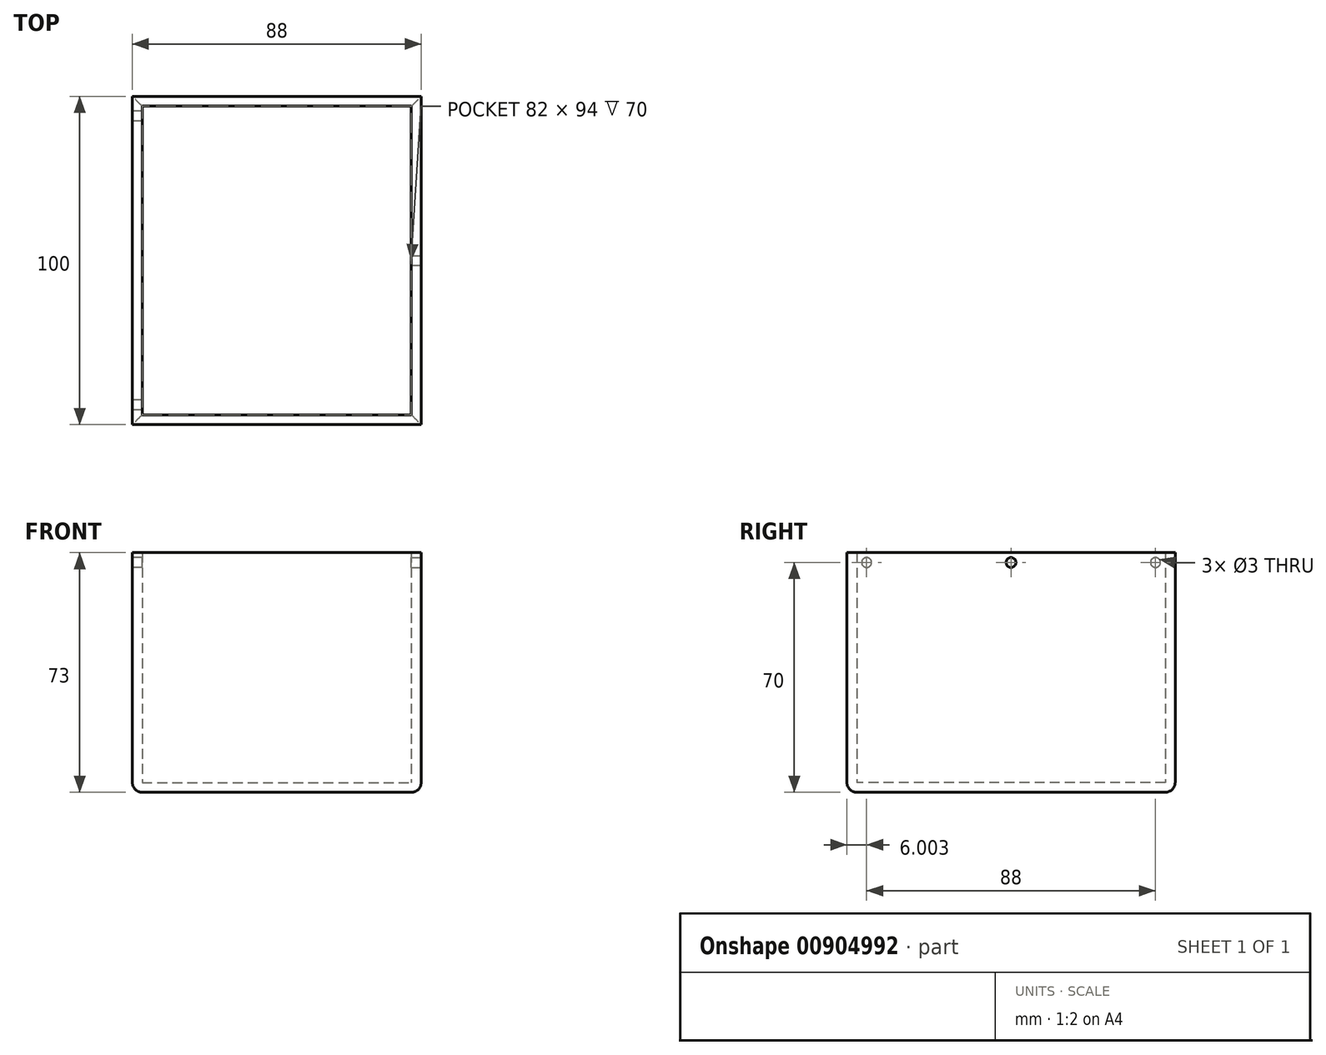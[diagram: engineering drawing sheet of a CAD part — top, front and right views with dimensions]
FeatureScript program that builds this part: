
annotation { "Feature Type Name" : "Feature", "Feature Type Description" : "" }
export const myFeature = defineFeature(function(context is Context, id is Id, definition is map)
    precondition{}
    {
        {
            var Q0;
            Q0=qCreatedBy(makeId("Top.planeOp"),FACE);
            var sketch = newSketch(context, id + "F0", { "sketchPlane" : qUnion([Q0])});
            skLineSegment(sketch, "E0.bottom", {"start": v(-35.32, 52.62) * mm, "end": v(52.68, 52.62) * mm});
            skLineSegment(sketch, "E0.top", {"start": v(-35.32, -47.38) * mm, "end": v(52.68, -47.38) * mm});
            skLineSegment(sketch, "E0.left", {"start": v(-35.32, 52.62) * mm, "end": v(-35.32, -47.38) * mm});
            skLineSegment(sketch, "E0.right", {"start": v(52.68, 52.62) * mm, "end": v(52.68, -47.38) * mm});
            skSolve(sketch);
        }
        {
            var Q0;
            Q0=makeQuery(id+"F0.imprint","IMPRINT",FACE,{"disambiguationData":[TD([[makeQuery(id+"F0.imprint","IMPRINT",EDGE,{"derivedFrom":sQuery(id+"F0.wireOp",EDGE,"E0.bottom")}),-1.0]])]});
            var sketch = newSketch(context, id + "F1", { "sketchPlane" : qUnion([Q0])});
            skLineSegment(sketch, "E1.0", {"start": v(-35.32, 52.62) * mm, "end": v(52.68, 52.62) * mm});
            skLineSegment(sketch, "E1.1", {"start": v(-35.32, 52.62) * mm, "end": v(-35.32, -47.38) * mm});
            skLineSegment(sketch, "E1.2", {"start": v(52.68, 52.62) * mm, "end": v(52.68, -47.38) * mm});
            skLineSegment(sketch, "E1.3", {"start": v(-35.32, -47.38) * mm, "end": v(52.68, -47.38) * mm});
            skLineSegment(sketch, "E2.bottom", {"start": v(-32.32, 49.62) * mm, "end": v(49.68, 49.62) * mm});
            skLineSegment(sketch, "E2.top", {"start": v(-32.32, -44.38) * mm, "end": v(49.68, -44.38) * mm});
            skLineSegment(sketch, "E2.left", {"start": v(-32.32, 49.62) * mm, "end": v(-32.32, -44.38) * mm});
            skLineSegment(sketch, "E2.right", {"start": v(49.68, 49.62) * mm, "end": v(49.68, -44.38) * mm});
            skSolve(sketch);
        }
        {
            var Q0;
            Q0 = qSketchRegion(id + "F0", true);
            extrude(context, id + "F2", {"entities" : qUnion([Q0]), "depth" : -3 * mm, "offsetDistance" : 25 * mm});
        }
        {
            var Q0;
            Q0 = qSketchRegion(id + "F1", true);
            extrude(context, id + "F3", {"entities" : qUnion([Q0]), "operationType" : NewBodyOperationType.ADD, "depth" : 70 * mm, "offsetDistance" : 25 * mm});
        }
        {
            var Q0;
            Q0=makeQuery(id+"F2.opExtrude","CAP_EDGE",EDGE,{"disambiguationData":[OSD([sQuery(id+"F0.wireOp",EDGE,"E0.left")])],"isStart":false});
            var Q1;
            Q1=makeQuery(id+"F2.opExtrude","CAP_EDGE",EDGE,{"disambiguationData":[OSD([sQuery(id+"F0.wireOp",EDGE,"E0.bottom")])],"isStart":false});
            var Q2;
            Q2=makeQuery(id+"F2.opExtrude","CAP_EDGE",EDGE,{"disambiguationData":[OSD([sQuery(id+"F0.wireOp",EDGE,"E0.top")])],"isStart":false});
            var Q3;
            Q3=makeQuery(id+"F2.opExtrude","CAP_EDGE",EDGE,{"disambiguationData":[OSD([sQuery(id+"F0.wireOp",EDGE,"E0.right")])],"isStart":false});
            fillet(context, id + "F4", {"entities" : qUnion([Q0, Q1, Q2, Q3]), "radius" : 3 * mm, "tangentPropagation" : true, "allowEdgeOverflow" : false});
        }
        {
            var Q0;
            Q0=makeQuery(id+"F3.boolean.opBoolean","MERGE",FACE,{"derivedFrom":[makeQuery(id+"F2.opExtrude","SWEPT_FACE",FACE,{"disambiguationData":[OSD([sQuery(id+"F0.wireOp",EDGE,"E0.left")])]}),makeQuery(id+"F3.opExtrude","SWEPT_FACE",FACE,{"disambiguationData":[OSD([sQuery(id+"F1.wireOp",EDGE,"E1.1")])]})]});
            var sketch = newSketch(context, id + "F5", { "sketchPlane" : qUnion([Q0])});
            skCircle(sketch, "E3", {"center": v(-46.62, 67) * mm, "radius": 1.5 * mm});
            skCircle(sketch, "E4", {"center": v(41.38, 67) * mm, "radius": 1.5 * mm});
            skSolve(sketch);
        }
        {
            var Q0;
            Q0 = qSketchRegion(id + "F5", true);
            extrude(context, id + "F6", {"entities" : qUnion([Q0]), "operationType" : NewBodyOperationType.REMOVE, "oppositeDirection" : true, "depth" : 25 * mm, "offsetDistance" : 25 * mm});
        }
        {
            var Q0;
            Q0=makeQuery(id+"F3.boolean.opBoolean","MERGE",FACE,{"derivedFrom":[makeQuery(id+"F2.opExtrude","SWEPT_FACE",FACE,{"disambiguationData":[OSD([sQuery(id+"F0.wireOp",EDGE,"E0.right")])]}),makeQuery(id+"F3.opExtrude","SWEPT_FACE",FACE,{"disambiguationData":[OSD([sQuery(id+"F1.wireOp",EDGE,"E1.2")])]})]});
            var sketch = newSketch(context, id + "F7", { "sketchPlane" : qUnion([Q0])});
            skLineSegment(sketch, "E5.0", {"start": v(52.62, 70) * mm, "end": v(-47.38, 70) * mm});
            skPoint(sketch, "E6", {"position": v(2.62, 70) * mm});
            skLineSegment(sketch, "E7", {"start": v(2.62, 70) * mm, "end": v(2.62, 67) * mm});
            skCircle(sketch, "E8", {"center": v(2.62, 67) * mm, "radius": 1.5 * mm});
            skSolve(sketch);
        }
        {
            var Q0;
            Q0 = qSketchRegion(id + "F7", true);
            extrude(context, id + "F8", {"entities" : qUnion([Q0]), "operationType" : NewBodyOperationType.REMOVE, "depth" : -25 * mm, "offsetDistance" : 25 * mm});
        }
    });
